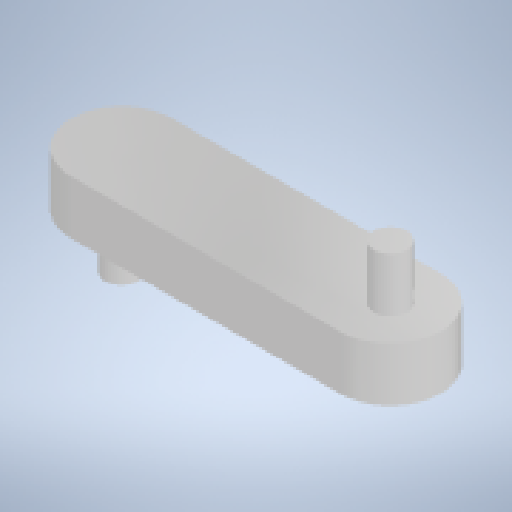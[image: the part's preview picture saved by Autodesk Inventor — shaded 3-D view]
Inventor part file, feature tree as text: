
AUTODESK INVENTOR PART (.ipt)
format: ipt  version: 2024 (Build 280153000, 153)  size: 239,616 bytes
history: native  units: in
note: dims shown in document units (in); Inventor stores cm internally (conversion verified against a paired STEP export)
features: extrude x3, sketch x3
ambient origin geometry x8: Origin, YZ Plane, XZ Plane, XY Plane, X Axis, Y Axis, Z Axis, Center Point
bodies: Solid1 (feature_tree)
feature tree (6):
  extrude  "Extrusion1"  Depth=0.75in
  extrude  "Extrusion4"  Depth=2.0in
  extrude  "Extrusion5"  Depth=0.75in
  sketch  "Sketch1"  dims[d1=2.0in d4=0.75in]
  sketch  "Sketch4"  dims[d6=0.4in d7=0.0in d14=2.0in]
  sketch  "Sketch5"  dims[d15=2.0in d16=0.75in d17=0.25in d18=0.4in d19=0.0in d20=0.25in d21=0.4in d22=0.0in d8=0.5in d9=0.0344in d10=0.5in d11=0.0344in]
